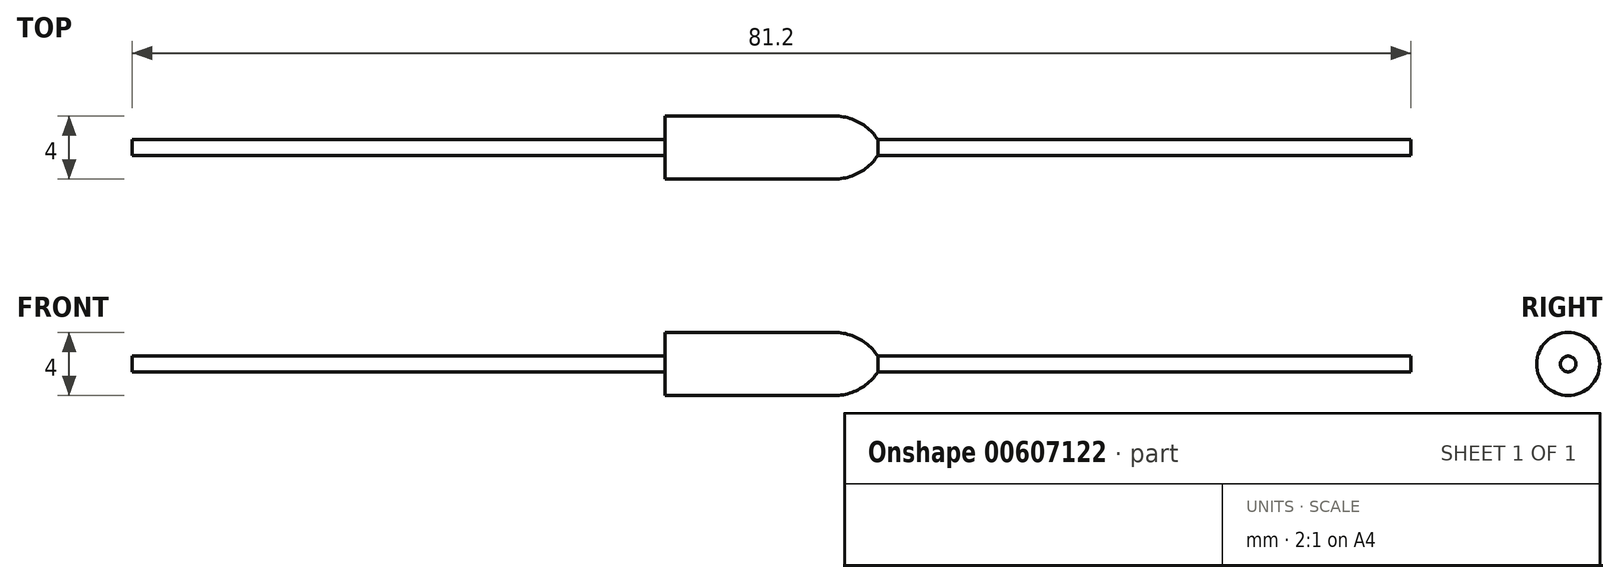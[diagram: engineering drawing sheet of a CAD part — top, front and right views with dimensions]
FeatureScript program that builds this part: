
annotation { "Feature Type Name" : "Feature", "Feature Type Description" : "" }
export const myFeature = defineFeature(function(context is Context, id is Id, definition is map)
    precondition{}
    {
        {
            var Q0;
            Q0=qCreatedBy(makeId("Front.planeOp"),FACE);
            var sketch = newSketch(context, id + "F0", { "sketchPlane" : qUnion([Q0])});
            skLineSegment(sketch, "E0.bottom", {"start": v(-40.6, 0) * mm, "end": v(0, 0) * mm});
            skLineSegment(sketch, "E0.top", {"start": v(-40.6, 0.5) * mm, "end": v(-6.75, 0.5) * mm});
            skLineSegment(sketch, "E0.left", {"start": v(-40.6, 0) * mm, "end": v(-40.6, 0.5) * mm});
            skLineSegment(sketch, "E1.bottom", {"start": v(-6.75, 0) * mm, "end": v(0, 0) * mm});
            skLineSegment(sketch, "E1.top", {"start": v(-6.75, 2) * mm, "end": v(0, 2) * mm});
            skLineSegment(sketch, "E1.left", {"start": v(-6.75, 0.5) * mm, "end": v(-6.75, 2) * mm});
            skLineSegment(sketch, "E2.MirrorCS", {"start": v(40.6, 0) * mm, "end": v(40.6, 0.5) * mm});
            skLineSegment(sketch, "E3.MirrorCS", {"start": v(40.6, 0) * mm, "end": v(0, 0) * mm});
            skLineSegment(sketch, "E4.MirrorCS", {"start": v(6.75, 0) * mm, "end": v(0, 0) * mm});
            skLineSegment(sketch, "E5.MirrorCS", {"start": v(4, 2) * mm, "end": v(0, 2) * mm});
            skLineSegment(sketch, "E6.MirrorCS", {"start": v(40.6, 0.5) * mm, "end": v(6.75, 0.5) * mm});
            skArc(sketch, "E7", {"start": v(6.75, 0.5) * mm, "mid": v(5.57, 1.6) * mm, "end": v(4, 2) * mm});
            skSolve(sketch);
        }
        {
            var Q0;
            Q0 = qSketchRegion(id + "F0", true);
            var Q1;
            Q1=sQuery(id+"F0.wireOp",EDGE,"E1.bottom");
            revolve(context, id + "F1", {"entities" : qUnion([Q0]), "axis" : qUnion([Q1]), "revolveType" : RevolveType.FULL});
        }
    });
